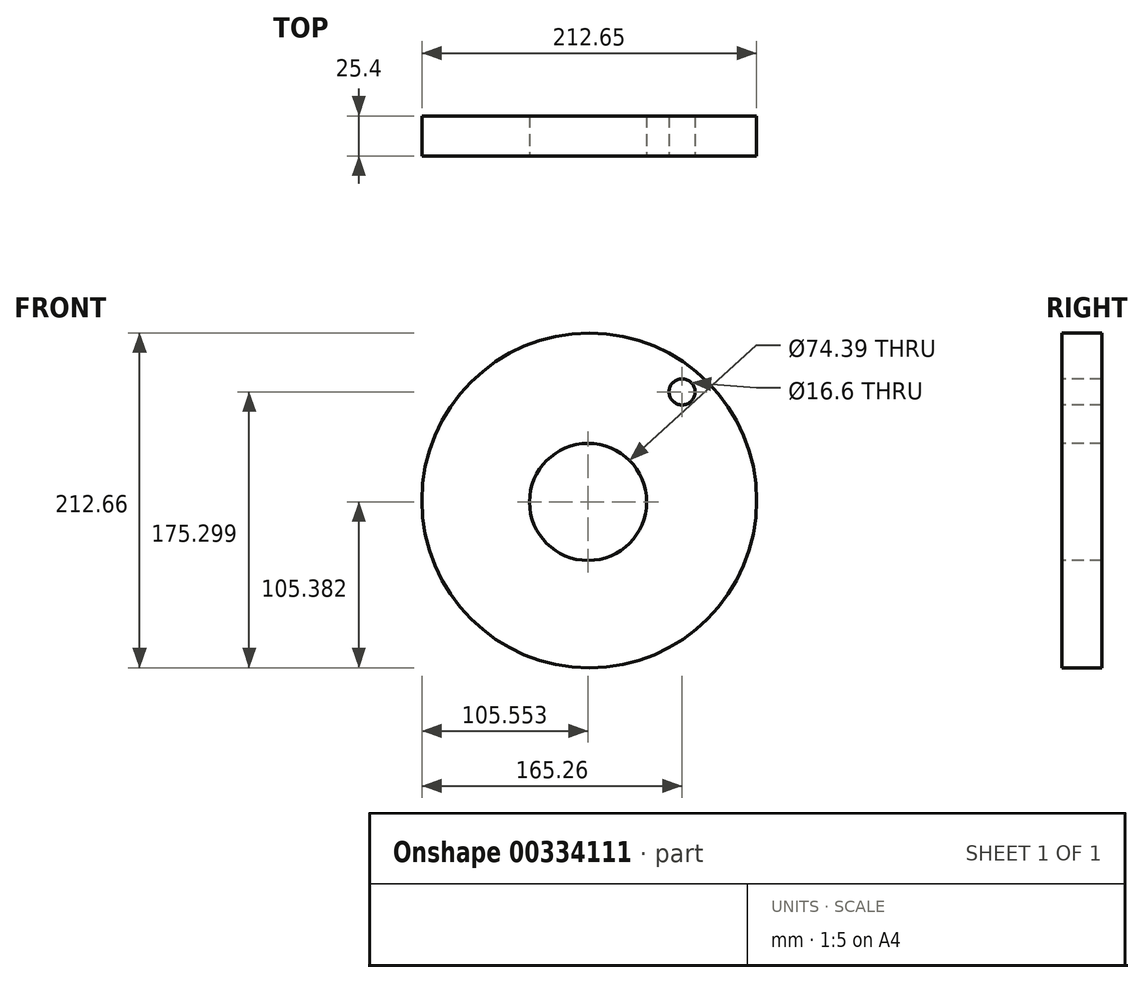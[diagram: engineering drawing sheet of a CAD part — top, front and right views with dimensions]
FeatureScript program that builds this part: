
annotation { "Feature Type Name" : "Feature", "Feature Type Description" : "" }
export const myFeature = defineFeature(function(context is Context, id is Id, definition is map)
    precondition{}
    {
        {
            var Q0;
            Q0=qCreatedBy(makeId("Front.planeOp"),FACE);
            var sketch = newSketch(context, id + "F0", { "sketchPlane" : qUnion([Q0])});
            skCircle(sketch, "E0", {"center": v(36.8, 0) * mm, "radius": 106.33 * mm});
            skSolve(sketch);
        }
        {
            var Q0;
            Q0=makeQuery(id+"F0.imprint","IMPRINT",FACE,{"disambiguationData":[TD([[makeQuery(id+"F0.imprint","IMPRINT",EDGE,{"derivedFrom":sQuery(id+"F0.wireOp",EDGE,"E0")}),1.0]])]});
            extrude(context, id + "F1", {"entities" : qUnion([Q0]), "depth" : 25.4 * mm});
        }
        {
            var Q0;
            Q0=makeQuery(id+"F1.opExtrude","CAP_FACE",FACE,{"disambiguationData":[OSD([sQuery(id+"F0.wireOp",EDGE,"E0")])],"isStart":false});
            var sketch = newSketch(context, id + "F2", { "sketchPlane" : qUnion([Q0])});
            skSolve(sketch);
        }
        {
            var Q0;
            Q0=makeQuery(id+"F2.imprint","IMPRINT",FACE,{"disambiguationData":[TD([[makeQuery(id+"F2.imprint","IMPRINT",EDGE,{"derivedFrom":makeQuery(id+"F1.opExtrude","CAP_EDGE",EDGE,{"disambiguationData":[OSD([sQuery(id+"F0.wireOp",EDGE,"E0")])],"isStart":false})}),1.0]])]});
            var sketch = newSketch(context, id + "F3", { "sketchPlane" : qUnion([Q0])});
            skCircle(sketch, "E1", {"center": v(36.02, -0.95) * mm, "radius": 37.2 * mm});
            skPoint(sketch, "E1.first.point", {"position": v(33.24, 36.14) * mm});
            skPoint(sketch, "E1.second.point", {"position": v(33, 36.13) * mm});
            skPoint(sketch, "E1.third.point", {"position": v(39.48, 36.09) * mm});
            skSolve(sketch);
        }
        {
            var Q0;
            Q0=makeQuery(id+"F3.imprint","IMPRINT",FACE,{"disambiguationData":[TD([[makeQuery(id+"F3.imprint","IMPRINT",EDGE,{"derivedFrom":sQuery(id+"F3.wireOp",EDGE,"E1")}),1.0]])]});
            extrude(context, id + "F4", {"entities" : qUnion([Q0]), "operationType" : NewBodyOperationType.REMOVE, "endBound" : BoundingType.THROUGH_ALL, "oppositeDirection" : true, "depth" : 25.4 * mm});
        }
        {
            var Q0;
            Q0=makeQuery(id+"F2.imprint","IMPRINT",FACE,{"disambiguationData":[TD([[makeQuery(id+"F2.imprint","IMPRINT",EDGE,{"derivedFrom":makeQuery(id+"F1.opExtrude","CAP_EDGE",EDGE,{"disambiguationData":[OSD([sQuery(id+"F0.wireOp",EDGE,"E0")])],"isStart":false})}),1.0]])]});
            var sketch = newSketch(context, id + "F5", { "sketchPlane" : qUnion([Q0])});
            skCircle(sketch, "E2", {"center": v(95.73, 68.97) * mm, "radius": 8.3 * mm});
            skSolve(sketch);
        }
        {
            var Q0;
            Q0 = qSketchRegion(id + "F5", true);
            extrude(context, id + "F6", {"entities" : qUnion([Q0]), "operationType" : NewBodyOperationType.REMOVE, "oppositeDirection" : true, "depth" : 25.4 * mm});
        }
    });
